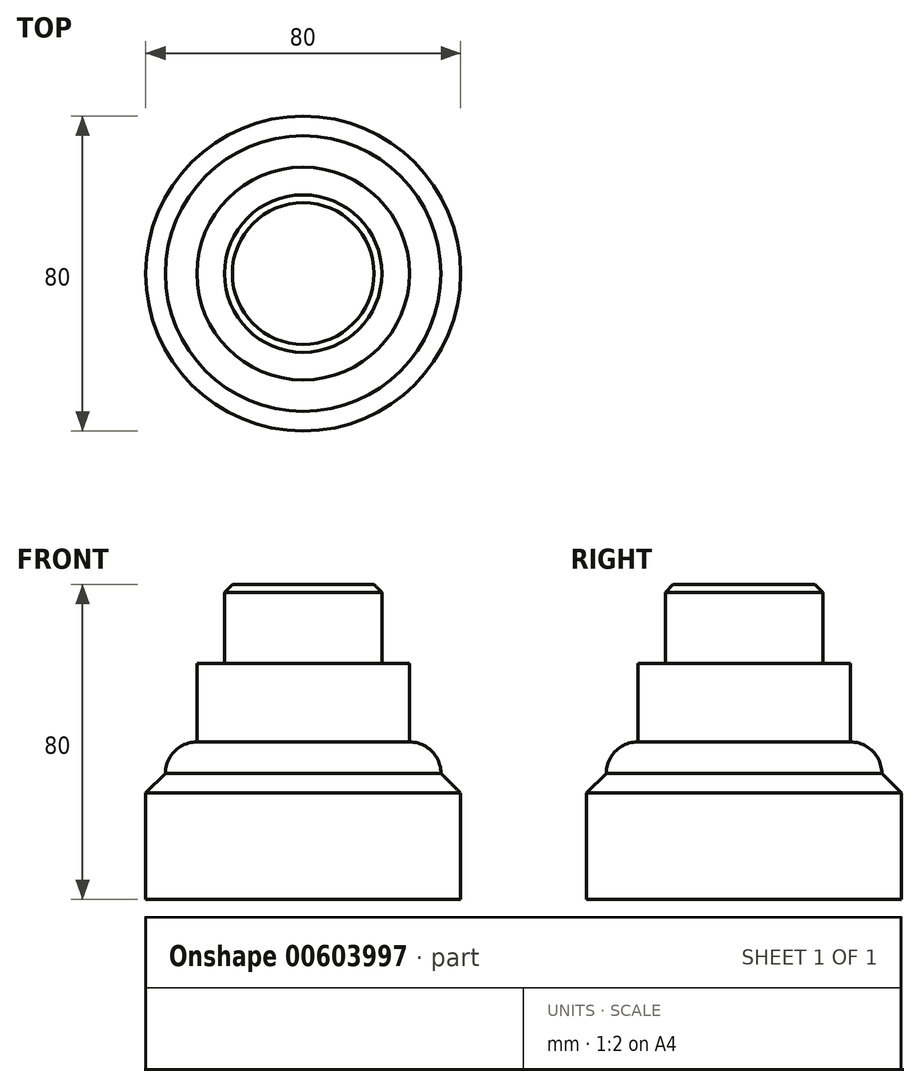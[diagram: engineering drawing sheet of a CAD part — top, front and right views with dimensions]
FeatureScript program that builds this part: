
annotation { "Feature Type Name" : "Feature", "Feature Type Description" : "" }
export const myFeature = defineFeature(function(context is Context, id is Id, definition is map)
    precondition{}
    {
        {
            var Q0;
            Q0=qCreatedBy(makeId("Front.planeOp"),FACE);
            var sketch = newSketch(context, id + "F0", { "sketchPlane" : qUnion([Q0])});
            skLineSegment(sketch, "E0", {"start": v(0, 0) * mm, "end": v(40, 0) * mm});
            skLineSegment(sketch, "E1", {"start": v(40, 0) * mm, "end": v(40, 27) * mm});
            skLineSegment(sketch, "E2", {"start": v(40, 27) * mm, "end": v(35, 32) * mm});
            skLineSegment(sketch, "E3", {"start": v(27, 40) * mm, "end": v(27, 60) * mm});
            skLineSegment(sketch, "E4", {"start": v(27, 60) * mm, "end": v(20, 60) * mm});
            skLineSegment(sketch, "E5", {"start": v(20, 60) * mm, "end": v(20, 78) * mm});
            skLineSegment(sketch, "E6", {"start": v(20, 78) * mm, "end": v(18, 80) * mm});
            skLineSegment(sketch, "E7", {"start": v(18, 80) * mm, "end": v(0, 80) * mm});
            skLineSegment(sketch, "E8", {"start": v(0, 80) * mm, "end": v(0, 0) * mm});
            skLineSegment(sketch, "E9", {"start": v(35, 32) * mm, "end": v(60.68, 32) * mm, "construction": true});
            skLineSegment(sketch, "E10", {"start": v(18, 80) * mm, "end": v(34.11, 80) * mm, "construction": true});
            skArc(sketch, "E11", {"start": v(35, 32) * mm, "mid": v(32.66, 37.66) * mm, "end": v(27, 40) * mm});
            skSolve(sketch);
        }
        {
            var Q0;
            Q0=makeQuery(id+"F0.imprint","IMPRINT",FACE,{"disambiguationData":[TD([[makeQuery(id+"F0.imprint","IMPRINT",EDGE,{"derivedFrom":sQuery(id+"F0.wireOp",EDGE,"E0")}),1.0]])]});
            var Q1;
            Q1=sQuery(id+"F0.wireOp",EDGE,"E8");
            revolve(context, id + "F1", {"entities" : qUnion([Q0]), "axis" : qUnion([Q1]), "revolveType" : RevolveType.FULL});
        }
    });
